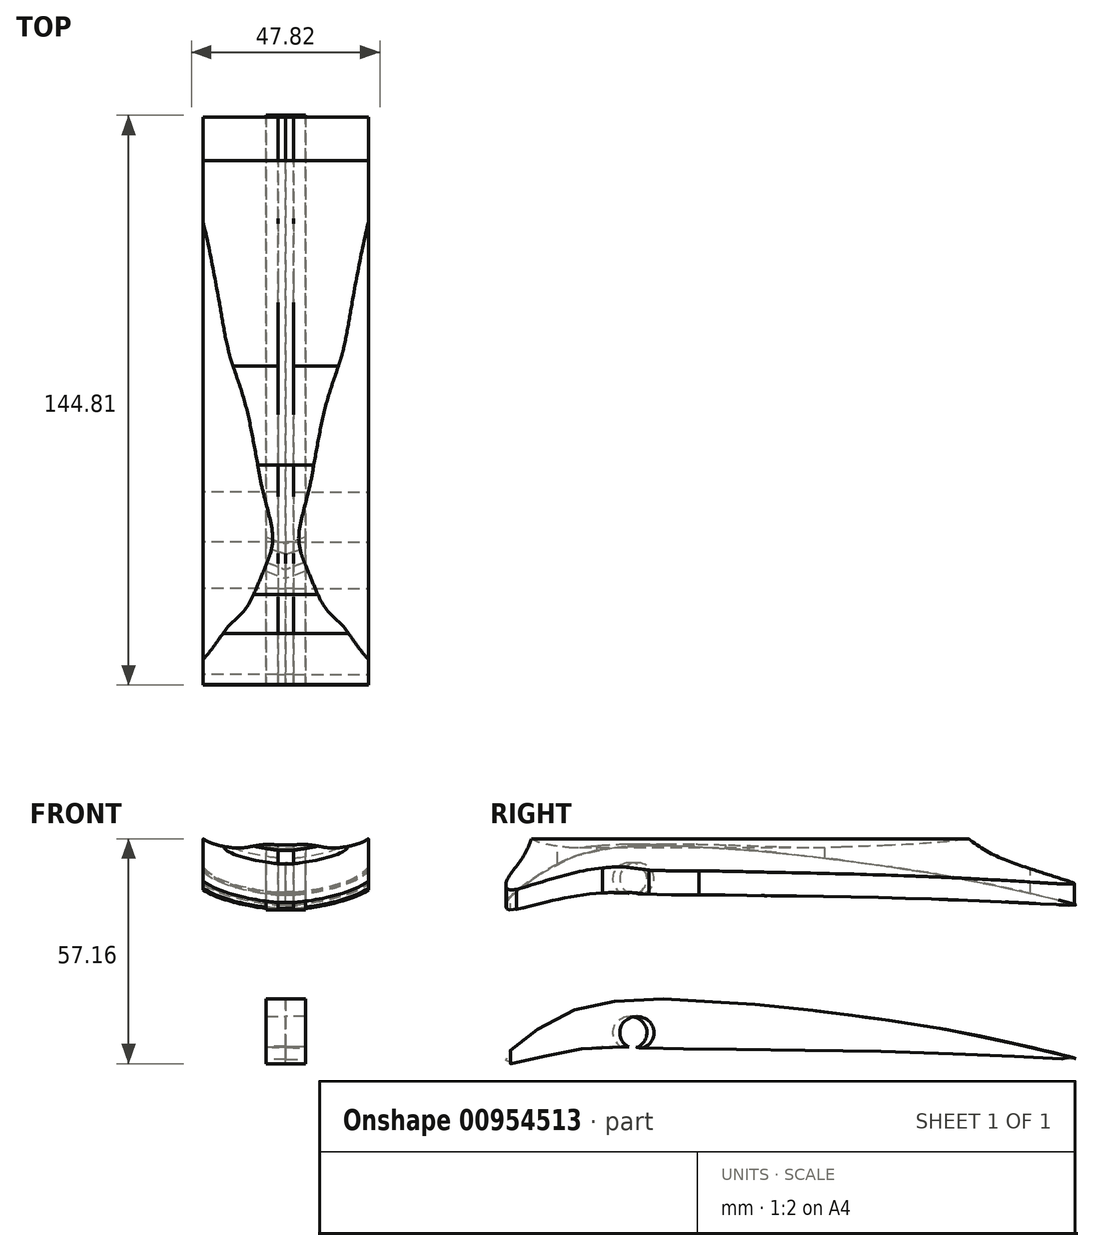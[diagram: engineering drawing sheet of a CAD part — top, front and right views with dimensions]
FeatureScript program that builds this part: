
annotation { "Feature Type Name" : "Feature", "Feature Type Description" : "" }
export const myFeature = defineFeature(function(context is Context, id is Id, definition is map)
    precondition{}
    {
        {
            var Q0;
            Q0=qCreatedBy(makeId("Right.planeOp"),FACE);
            var sketch = newSketch(context, id + "F0", { "sketchPlane" : qUnion([Q0])});
            skLineSegment(sketch, "E0", {"start": v(-72.17, 38.9) * mm, "end": v(77.83, 38.9) * mm});
            skFitSpline(sketch, "E1", {"points": [v(-68.8, 12.14) * mm, v(-68.05, 13.99) * mm, v(-64.01, 17.6) * mm, v(-54.5, 23.41) * mm, v(-45.58, 26.27) * mm, v(-31.78, 27.54) * mm, v(-16.55, 26.86) * mm, v(-5.03, 26.1) * mm, v(18.7, 23.41) * mm, v(47.3, 18.95) * mm, v(73.06, 13.23) * mm, v(76, 12.3) * mm, v(73.56, 12.3) * mm, v(60.1, 12.98) * mm, v(33.42, 13.99) * mm, v(-1.4, 14.66) * mm, v(-22.7, 14.91) * mm, v(-33.13, 15.08) * mm, v(-43.9, 15.42) * mm, v(-53.91, 14.07) * mm, v(-62.66, 12.05) * mm, v(-68.22, 11.21) * mm, v(-68.8, 12.14) * mm]});
            skLineSegment(sketch, "E2", {"start": v(-39.08, 15.39) * mm, "end": v(-35.4, 15.2) * mm});
            skSolve(sketch);
        }
        {
            var Q0;
            Q0=makeQuery(id+"F0.imprint","IMPRINT",FACE,{"disambiguationData":[TD([[makeQuery(id+"F0.imprint","IMPRINT",EDGE,{"derivedFrom":sQuery(id+"F0.wireOp",EDGE,"E1")}),-1.0]])]});
            extrude(context, id + "F1", {"entities" : qUnion([Q0]), "depth" : 5 * mm, "offsetDistance" : 25 * mm});
        }
        {
            var Q0;
            Q0=qCreatedBy(makeId("Top.planeOp"),FACE);
            var sketch = newSketch(context, id + "F2", { "sketchPlane" : qUnion([Q0])});
            skLineSegment(sketch, "E3", {"start": v(5, -36.1) * mm, "end": v(-1, -38.29) * mm});
            skLineSegment(sketch, "E4", {"start": v(5, -36.1) * mm, "end": v(-1, -36.1) * mm, "construction": true});
            skLineSegment(sketch, "E5", {"start": v(-1, -36.1) * mm, "end": v(-1, -38.29) * mm, "construction": true});
            skSolve(sketch);
        }
        {
            var Q0;
            Q0=sQuery(id+"F2.wireOp",VERTEX,"E3.start");
            var Q1;
            Q1=sQuery(id+"F2.wireOp",EDGE,"E3");
            cPlane(context, id + "F3", {"entities" : qUnion([Q0, Q1]), "cplaneType" : CPlaneType.LINE_POINT, "offset" : 25 * mm, "width" : 150 * mm, "height" : 150 * mm});
        }
        {
            var Q0;
            Q0=qCreatedBy(id+"F3.planeOp",FACE);
            var sketch = newSketch(context, id + "F4", { "sketchPlane" : qUnion([Q0])});
            skCircle(sketch, "E6", {"center": v(35.06, 18.96) * mm, "radius": 4.1 * mm});
            skSolve(sketch);
        }
        {
            var Q0;
            Q0 = qSketchRegion(id + "F4", true);
            extrude(context, id + "F5", {"entities" : qUnion([Q0]), "operationType" : NewBodyOperationType.REMOVE, "oppositeDirection" : true, "depth" : 11.7 * mm, "offsetDistance" : 25 * mm, "hasSecondDirection" : true, "secondDirectionOppositeDirection" : false, "secondDirectionDepth" : 25 * mm});
        }
        {
            var Q0;
            Q0=makeQuery(id+"F1.opExtrude","SWEPT_BODY",BODY,{"disambiguationData":[OSD([sQuery(id+"F0.wireOp",EDGE,"E1"),sQuery(id+"F0.wireOp",EDGE,"E2")])]});
            var Q1;
            Q1=qCreatedBy(makeId("Right.planeOp"),FACE);
            mirror(context, id + "F6", {"entities" : qUnion([Q0]), "mirrorPlane" : qUnion([Q1])});
        }
        {
            var Q0;
            Q0=makeQuery(id+"F1.opExtrude","SWEPT_BODY",BODY,{"disambiguationData":[OSD([sQuery(id+"F0.wireOp",EDGE,"E1"),sQuery(id+"F0.wireOp",EDGE,"E2")])]});
            transform(context, id + "F7", {"entities" : qUnion([Q0]), "transformType" : TransformType.TRANSLATION_3D, "dx" : 0 * mm, "dy" : 0 * mm, "dz" : 39.1 * mm, "makeCopy" : true});
        }
        {
            var Q0;
            Q0=makeQuery(id+"F7.opPattern","COPY",FACE,{"derivedFrom":makeQuery(id+"F1.opExtrude","CAP_FACE",FACE,{"disambiguationData":[OSD([sQuery(id+"F0.wireOp",EDGE,"E1"),sQuery(id+"F0.wireOp",EDGE,"E2")])],"isStart":true}),"instanceName":"1"});
            var sketch = newSketch(context, id + "F8", { "sketchPlane" : qUnion([Q0])});
            skFitSpline(sketch, "E7", {"points": [v(68.63, 52.07) * mm, v(55.71, 61.9) * mm, v(45.8, 65.33) * mm, v(35.3, 66.54) * mm, v(20.84, 66.24) * mm, v(0, 64.73) * mm, v(-12.3, 63.32) * mm, v(-28.43, 61.2) * mm, v(-48.44, 57.83) * mm, v(-64.52, 54.39) * mm, v(-75.58, 51.63) * mm, v(-65.82, 51.8) * mm, v(-46.23, 52.67) * mm, v(-33.95, 53.07) * mm, v(-14.6, 53.5) * mm, v(2.5, 53.78) * mm, v(19.78, 54) * mm, v(32.4, 54.15) * mm, v(44.27, 54.5) * mm, v(66.12, 50.34) * mm, v(68.59, 50.57) * mm, v(68.63, 52.07) * mm]});
            skSolve(sketch);
        }
        {
            var Q0;
            {var subQ0=sQuery(id+"F8.wireOp",EDGE,"E7");var subQ1=makeQuery(id+"F7.opPattern","COPY",EDGE,{"derivedFrom":makeQuery(id+"F5.boolean.opBoolean","INTERSECT",EDGE,{"derivedFrom":[makeQuery(id+"F1.opExtrude","CAP_FACE",FACE,{"disambiguationData":[OSD([sQuery(id+"F0.wireOp",EDGE,"E1"),sQuery(id+"F0.wireOp",EDGE,"E2")])],"isStart":true}),makeQuery(id+"F5.opExtrude","SWEPT_FACE",FACE,{"disambiguationData":[OSD([sQuery(id+"F4.wireOp",EDGE,"E6")])]})]}),"instanceName":"1"});var subQ2=makeQuery(id+"F8.imprint","INTERSECT",VERTEX,{"disambiguationData":[OD(0.0)],"derivedFrom":[subQ1,subQ0]});var subQ3=makeQuery(id+"F8.imprint","INTERSECT",VERTEX,{"disambiguationData":[OD(1.0)],"derivedFrom":[subQ1,subQ0]});Q0=makeQuery(id+"F8.imprint","IMPRINT",FACE,{"disambiguationData":[TD([[makeQuery(id+"F8.imprint","IMPRINT",EDGE,{"disambiguationData":[TD([[subQ2,-1.0],[subQ3,1.0]])],"derivedFrom":subQ0}),1.0]])]});}
            var Q1;
            {var subQ0=sQuery(id+"F8.wireOp",EDGE,"E7");var subQ1=sQuery(id+"F0.wireOp",EDGE,"E1");var subQ5=makeQuery(id+"F7.opPattern","COPY",EDGE,{"derivedFrom":makeQuery(id+"F1.opExtrude","CAP_EDGE",EDGE,{"disambiguationData":[OSD([subQ1])],"isStart":true}),"instanceName":"1"});var subQ34=makeQuery(id+"F8.imprint","INTERSECT",VERTEX,{"disambiguationData":[OD(12.0)],"derivedFrom":[subQ5,subQ0]});var subQ35=makeQuery(id+"F8.imprint","INTERSECT",VERTEX,{"disambiguationData":[OD(13.0)],"derivedFrom":[subQ5,subQ0]});Q1=makeQuery(id+"F8.imprint","IMPRINT",FACE,{"disambiguationData":[TD([[makeQuery(id+"F8.imprint","IMPRINT",EDGE,{"disambiguationData":[TD([[subQ34,1.0],[subQ35,-1.0]])],"derivedFrom":subQ0}),1.0]])]});}
            extrude(context, id + "F9", {"entities" : qUnion([Q0, Q1]), "operationType" : NewBodyOperationType.ADD, "depth" : 2 * mm, "offsetDistance" : 25 * mm});
        }
        {
            var Q0;
            Q0=qCreatedBy(makeId("Front.planeOp"),FACE);
            var sketch = newSketch(context, id + "F10", { "sketchPlane" : qUnion([Q0])});
            skFitSpline(sketch, "E8.MirrorCS", {"points": [v(-2, 55.84) * mm, v(-17.8, 59.88) * mm, v(-22.48, 66.42) * mm, v(-22.95, 68.25) * mm], "startDerivative": vector(-7.82, 0.46) * mm, "endDerivative": vector(-2.8, 13.39) * mm});
            skSolve(sketch);
        }
        {
            var Q0;
            Q0=makeQuery(id+"F9.opExtrude","CAP_FACE",FACE,{"disambiguationData":[OSD([sQuery(id+"F0.wireOp",EDGE,"E1"),sQuery(id+"F8.wireOp",EDGE,"a6976920-849d-4efb-921a-e7d622ed5d83")])],"isStart":false});
            var Q1;
            Q1=sQuery(id+"F10.wireOp",EDGE,"E8.MirrorCS");
            sweep(context, id + "F11", {"operationType" : NewBodyOperationType.ADD, "profiles" : qUnion([Q0]), "path" : qUnion([Q1])});
        }
        {
            var Q0;
            Q0=qCreatedBy(makeId("Front.planeOp"),FACE);
            var sketch = newSketch(context, id + "F12", { "sketchPlane" : qUnion([Q0])});
            skLineSegment(sketch, "E9", {"start": v(25.67, 71.86) * mm, "end": v(25.67, 27.3) * mm});
            skSolve(sketch);
        }
        {
            var Q0;
            Q0=qCreatedBy(makeId("Front.planeOp"),FACE);
            var sketch = newSketch(context, id + "F13", { "sketchPlane" : qUnion([Q0])});
            skFitSpline(sketch, "E10", {"points": [v(-1.13, 66.75) * mm, v(-6.55, 66.66) * mm, v(-11.78, 65.9) * mm, v(-19.16, 67.26) * mm, v(-21.73, 69.18) * mm, v(-21.97, 70.11) * mm, v(-21.87, 70.02) * mm, v(-21.31, 70.44) * mm], "startDerivative": vector(-27.1, 0.93) * mm, "endDerivative": vector(9.07, 9.45) * mm});
            skLineSegment(sketch, "E11", {"start": v(-20.98, 53.3) * mm, "end": v(-20.98, 68.26) * mm});
            skLineSegment(sketch, "E12", {"start": v(-1.13, 66.75) * mm, "end": v(-3.65, 70.77) * mm});
            skLineSegment(sketch, "E13", {"start": v(-3.65, 70.77) * mm, "end": v(-17.57, 71.51) * mm});
            skLineSegment(sketch, "E14", {"start": v(-17.57, 71.51) * mm, "end": v(-29.72, 69.37) * mm});
            skLineSegment(sketch, "E15", {"start": v(-29.72, 69.37) * mm, "end": v(-28.46, 56.38) * mm});
            skLineSegment(sketch, "E16", {"start": v(-28.46, 56.38) * mm, "end": v(-20.98, 53.3) * mm});
            skSolve(sketch);
        }
        {
            var Q0;
            Q0=makeQuery(id+"F13.imprint","IMPRINT",FACE,{"disambiguationData":[TD([[makeQuery(id+"F13.imprint","IMPRINT",EDGE,{"derivedFrom":sQuery(id+"F13.wireOp",EDGE,"E10")}),-1.0]])]});
            extrude(context, id + "F14", {"entities" : qUnion([Q0]), "operationType" : NewBodyOperationType.REMOVE, "oppositeDirection" : true, "depth" : 80 * mm, "offsetDistance" : 25 * mm, "hasSecondDirection" : true, "secondDirectionOppositeDirection" : false, "secondDirectionDepth" : 80 * mm});
        }
        {
            var Q0;
            Q0=makeQuery(id+"F7.opPattern","COPY",BODY,{"derivedFrom":makeQuery(id+"F1.opExtrude","SWEPT_BODY",BODY,{"disambiguationData":[OSD([sQuery(id+"F0.wireOp",EDGE,"E1"),sQuery(id+"F0.wireOp",EDGE,"E2")])]}),"instanceName":"1"});
            var Q1;
            Q1=qCreatedBy(makeId("Right.planeOp"),FACE);
            mirror(context, id + "F15", {"entities" : qUnion([Q0]), "mirrorPlane" : qUnion([Q1])});
        }
    });
